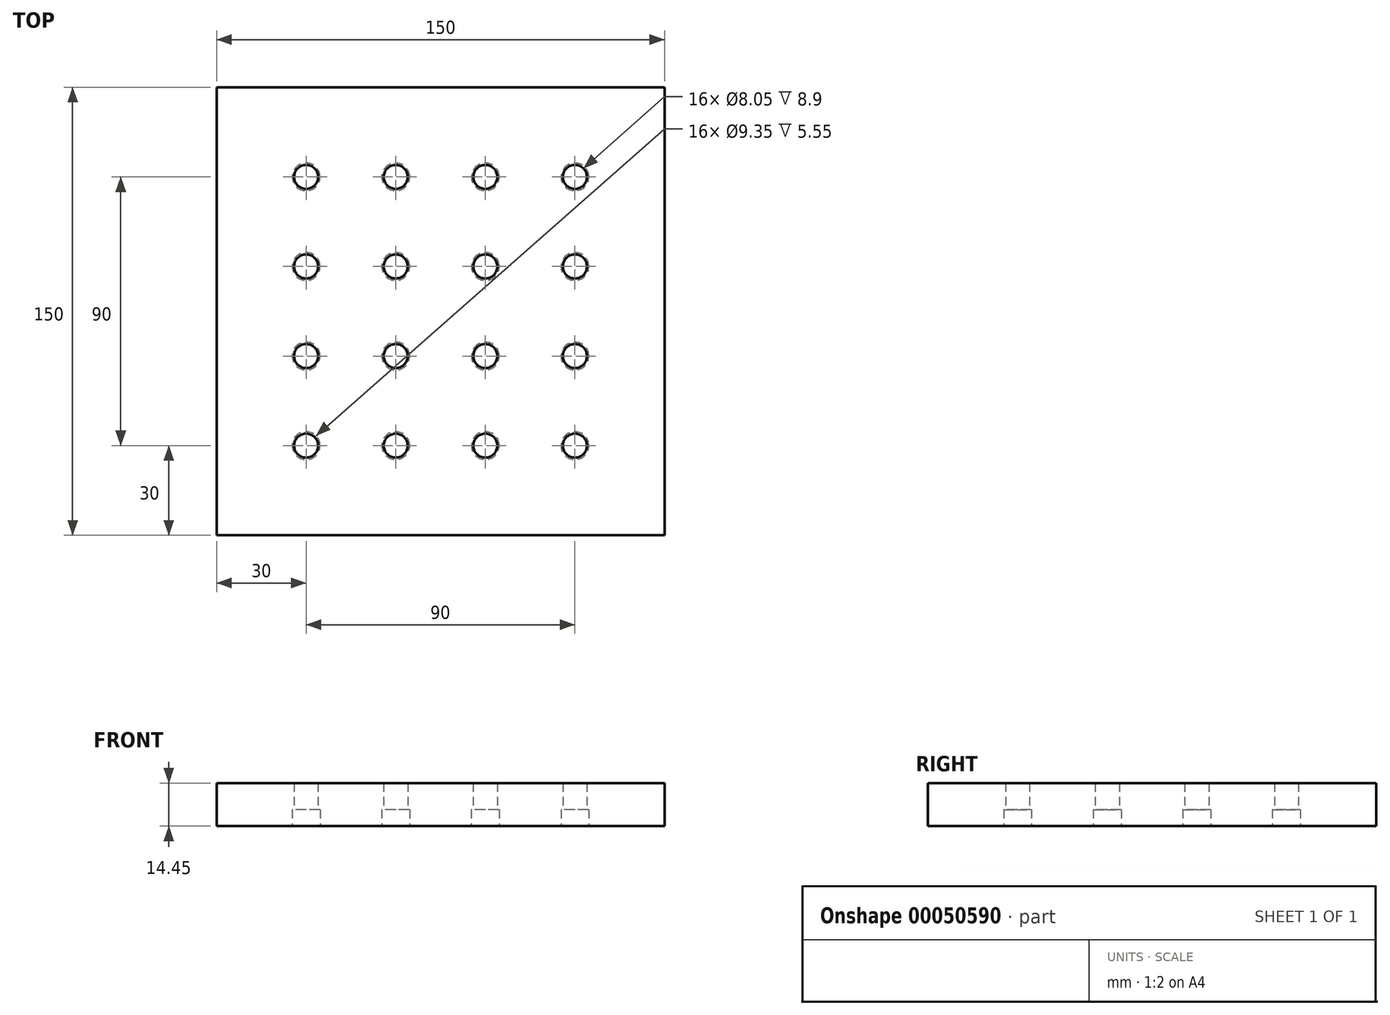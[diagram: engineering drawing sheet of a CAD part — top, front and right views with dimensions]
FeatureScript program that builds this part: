
annotation { "Feature Type Name" : "Feature", "Feature Type Description" : "" }
export const myFeature = defineFeature(function(context is Context, id is Id, definition is map)
    precondition{}
    {
        {
            var Q0;
            Q0=qCreatedBy(makeId("Top.planeOp"),FACE);
            var sketch = newSketch(context, id + "F0", { "sketchPlane" : qUnion([Q0])});
            skLineSegment(sketch, "E0.bottom", {"start": v(0, 0) * mm, "end": v(-150, 0) * mm});
            skLineSegment(sketch, "E0.top", {"start": v(0, 150) * mm, "end": v(-150, 150) * mm});
            skLineSegment(sketch, "E0.left", {"start": v(0, 0) * mm, "end": v(0, 150) * mm});
            skLineSegment(sketch, "E0.right", {"start": v(-150, 0) * mm, "end": v(-150, 150) * mm});
            skCircle(sketch, "E1", {"center": v(-120, 30) * mm, "radius": 4.68 * mm});
            skCircle(sketch, "E2", {"center": v(-120, 30) * mm, "radius": 4.03 * mm});
            skCircle(sketch, "E3.0.1.0", {"center": v(-120, 60) * mm, "radius": 4.68 * mm});
            skCircle(sketch, "E3.0.1.1", {"center": v(-120, 60) * mm, "radius": 4.03 * mm});
            skCircle(sketch, "E3.0.2.0", {"center": v(-120, 90) * mm, "radius": 4.68 * mm});
            skCircle(sketch, "E3.0.2.1", {"center": v(-120, 90) * mm, "radius": 4.03 * mm});
            skCircle(sketch, "E3.0.3.0", {"center": v(-120, 120) * mm, "radius": 4.68 * mm});
            skCircle(sketch, "E3.0.3.1", {"center": v(-120, 120) * mm, "radius": 4.03 * mm});
            skCircle(sketch, "E3.1.0.0", {"center": v(-90, 30) * mm, "radius": 4.68 * mm});
            skCircle(sketch, "E3.1.0.1", {"center": v(-90, 30) * mm, "radius": 4.03 * mm});
            skCircle(sketch, "E3.1.1.0", {"center": v(-90, 60) * mm, "radius": 4.68 * mm});
            skCircle(sketch, "E3.1.1.1", {"center": v(-90, 60) * mm, "radius": 4.03 * mm});
            skCircle(sketch, "E3.1.2.0", {"center": v(-90, 90) * mm, "radius": 4.68 * mm});
            skCircle(sketch, "E3.1.2.1", {"center": v(-90, 90) * mm, "radius": 4.03 * mm});
            skCircle(sketch, "E3.1.3.0", {"center": v(-90, 120) * mm, "radius": 4.68 * mm});
            skCircle(sketch, "E3.1.3.1", {"center": v(-90, 120) * mm, "radius": 4.03 * mm});
            skCircle(sketch, "E3.2.0.0", {"center": v(-60, 30) * mm, "radius": 4.68 * mm});
            skCircle(sketch, "E3.2.0.1", {"center": v(-60, 30) * mm, "radius": 4.03 * mm});
            skCircle(sketch, "E3.2.1.0", {"center": v(-60, 60) * mm, "radius": 4.68 * mm});
            skCircle(sketch, "E3.2.1.1", {"center": v(-60, 60) * mm, "radius": 4.03 * mm});
            skCircle(sketch, "E3.2.2.0", {"center": v(-60, 90) * mm, "radius": 4.68 * mm});
            skCircle(sketch, "E3.2.2.1", {"center": v(-60, 90) * mm, "radius": 4.03 * mm});
            skCircle(sketch, "E3.2.3.0", {"center": v(-60, 120) * mm, "radius": 4.68 * mm});
            skCircle(sketch, "E3.2.3.1", {"center": v(-60, 120) * mm, "radius": 4.03 * mm});
            skCircle(sketch, "E3.3.0.0", {"center": v(-30, 30) * mm, "radius": 4.68 * mm});
            skCircle(sketch, "E3.3.0.1", {"center": v(-30, 30) * mm, "radius": 4.03 * mm});
            skCircle(sketch, "E3.3.1.0", {"center": v(-30, 60) * mm, "radius": 4.68 * mm});
            skCircle(sketch, "E3.3.1.1", {"center": v(-30, 60) * mm, "radius": 4.03 * mm});
            skCircle(sketch, "E3.3.2.0", {"center": v(-30, 90) * mm, "radius": 4.68 * mm});
            skCircle(sketch, "E3.3.2.1", {"center": v(-30, 90) * mm, "radius": 4.03 * mm});
            skCircle(sketch, "E3.3.3.0", {"center": v(-30, 120) * mm, "radius": 4.68 * mm});
            skCircle(sketch, "E3.3.3.1", {"center": v(-30, 120) * mm, "radius": 4.03 * mm});
            skLineSegment(sketch, "E3.direction1", {"start": v(-120, 30) * mm, "end": v(-90, 30) * mm, "construction": true});
            skLineSegment(sketch, "E3.direction2", {"start": v(-120, 30) * mm, "end": v(-120, 60) * mm, "construction": true});
            skSolve(sketch);
        }
        {
            var Q0;
            Q0=makeQuery(id+"F0.imprint","IMPRINT",FACE,{"disambiguationData":[TD([[makeQuery(id+"F0.imprint","IMPRINT",EDGE,{"derivedFrom":sQuery(id+"F0.wireOp",EDGE,"E3.0.3.1")}),1.0]])]});
            var Q1;
            Q1=makeQuery(id+"F0.imprint","IMPRINT",FACE,{"disambiguationData":[TD([[makeQuery(id+"F0.imprint","IMPRINT",EDGE,{"derivedFrom":sQuery(id+"F0.wireOp",EDGE,"E3.1.3.1")}),1.0]])]});
            var Q2;
            Q2=makeQuery(id+"F0.imprint","IMPRINT",FACE,{"disambiguationData":[TD([[makeQuery(id+"F0.imprint","IMPRINT",EDGE,{"derivedFrom":sQuery(id+"F0.wireOp",EDGE,"E3.2.3.1")}),1.0]])]});
            var Q3;
            Q3=makeQuery(id+"F0.imprint","IMPRINT",FACE,{"disambiguationData":[TD([[makeQuery(id+"F0.imprint","IMPRINT",EDGE,{"derivedFrom":sQuery(id+"F0.wireOp",EDGE,"E3.3.2.1")}),1.0]])]});
            var Q4;
            Q4=makeQuery(id+"F0.imprint","IMPRINT",FACE,{"disambiguationData":[TD([[makeQuery(id+"F0.imprint","IMPRINT",EDGE,{"derivedFrom":sQuery(id+"F0.wireOp",EDGE,"E3.2.2.1")}),1.0]])]});
            var Q5;
            Q5=makeQuery(id+"F0.imprint","IMPRINT",FACE,{"disambiguationData":[TD([[makeQuery(id+"F0.imprint","IMPRINT",EDGE,{"derivedFrom":sQuery(id+"F0.wireOp",EDGE,"E3.1.2.1")}),1.0]])]});
            var Q6;
            Q6=makeQuery(id+"F0.imprint","IMPRINT",FACE,{"disambiguationData":[TD([[makeQuery(id+"F0.imprint","IMPRINT",EDGE,{"derivedFrom":sQuery(id+"F0.wireOp",EDGE,"E3.0.1.1")}),1.0]])]});
            var Q7;
            Q7=makeQuery(id+"F0.imprint","IMPRINT",FACE,{"disambiguationData":[TD([[makeQuery(id+"F0.imprint","IMPRINT",EDGE,{"derivedFrom":sQuery(id+"F0.wireOp",EDGE,"E3.1.1.1")}),1.0]])]});
            var Q8;
            Q8=makeQuery(id+"F0.imprint","IMPRINT",FACE,{"disambiguationData":[TD([[makeQuery(id+"F0.imprint","IMPRINT",EDGE,{"derivedFrom":sQuery(id+"F0.wireOp",EDGE,"E3.2.1.1")}),1.0]])]});
            var Q9;
            Q9=makeQuery(id+"F0.imprint","IMPRINT",FACE,{"disambiguationData":[TD([[makeQuery(id+"F0.imprint","IMPRINT",EDGE,{"derivedFrom":sQuery(id+"F0.wireOp",EDGE,"E3.3.1.1")}),1.0]])]});
            var Q10;
            Q10=makeQuery(id+"F0.imprint","IMPRINT",FACE,{"disambiguationData":[TD([[makeQuery(id+"F0.imprint","IMPRINT",EDGE,{"derivedFrom":sQuery(id+"F0.wireOp",EDGE,"E3.3.0.1")}),1.0]])]});
            var Q11;
            Q11=makeQuery(id+"F0.imprint","IMPRINT",FACE,{"disambiguationData":[TD([[makeQuery(id+"F0.imprint","IMPRINT",EDGE,{"derivedFrom":sQuery(id+"F0.wireOp",EDGE,"E3.2.0.1")}),1.0]])]});
            var Q12;
            Q12=makeQuery(id+"F0.imprint","IMPRINT",FACE,{"disambiguationData":[TD([[makeQuery(id+"F0.imprint","IMPRINT",EDGE,{"derivedFrom":sQuery(id+"F0.wireOp",EDGE,"E3.1.0.1")}),1.0]])]});
            var Q13;
            Q13=makeQuery(id+"F0.imprint","IMPRINT",FACE,{"disambiguationData":[TD([[makeQuery(id+"F0.imprint","IMPRINT",EDGE,{"derivedFrom":sQuery(id+"F0.wireOp",EDGE,"E3.0.3.0")}),1.0]])]});
            var Q14;
            Q14=makeQuery(id+"F0.imprint","IMPRINT",FACE,{"disambiguationData":[TD([[makeQuery(id+"F0.imprint","IMPRINT",EDGE,{"derivedFrom":sQuery(id+"F0.wireOp",EDGE,"E3.1.3.0")}),1.0]])]});
            var Q15;
            Q15=makeQuery(id+"F0.imprint","IMPRINT",FACE,{"disambiguationData":[TD([[makeQuery(id+"F0.imprint","IMPRINT",EDGE,{"derivedFrom":sQuery(id+"F0.wireOp",EDGE,"E3.1.2.0")}),1.0]])]});
            var Q16;
            Q16=makeQuery(id+"F0.imprint","IMPRINT",FACE,{"disambiguationData":[TD([[makeQuery(id+"F0.imprint","IMPRINT",EDGE,{"derivedFrom":sQuery(id+"F0.wireOp",EDGE,"E3.2.3.0")}),1.0]])]});
            var Q17;
            Q17=makeQuery(id+"F0.imprint","IMPRINT",FACE,{"disambiguationData":[TD([[makeQuery(id+"F0.imprint","IMPRINT",EDGE,{"derivedFrom":sQuery(id+"F0.wireOp",EDGE,"E3.2.2.0")}),1.0]])]});
            var Q18;
            Q18=makeQuery(id+"F0.imprint","IMPRINT",FACE,{"disambiguationData":[TD([[makeQuery(id+"F0.imprint","IMPRINT",EDGE,{"derivedFrom":sQuery(id+"F0.wireOp",EDGE,"E3.0.2.1")}),1.0]])]});
            var Q19;
            Q19=makeQuery(id+"F0.imprint","IMPRINT",FACE,{"disambiguationData":[TD([[makeQuery(id+"F0.imprint","IMPRINT",EDGE,{"derivedFrom":sQuery(id+"F0.wireOp",EDGE,"E3.0.2.0")}),1.0]])]});
            var Q20;
            Q20=makeQuery(id+"F0.imprint","IMPRINT",FACE,{"disambiguationData":[TD([[makeQuery(id+"F0.imprint","IMPRINT",EDGE,{"derivedFrom":sQuery(id+"F0.wireOp",EDGE,"E3.3.3.0")}),1.0]])]});
            var Q21;
            Q21=makeQuery(id+"F0.imprint","IMPRINT",FACE,{"disambiguationData":[TD([[makeQuery(id+"F0.imprint","IMPRINT",EDGE,{"derivedFrom":sQuery(id+"F0.wireOp",EDGE,"E3.3.3.1")}),1.0]])]});
            var Q22;
            Q22=makeQuery(id+"F0.imprint","IMPRINT",FACE,{"disambiguationData":[TD([[makeQuery(id+"F0.imprint","IMPRINT",EDGE,{"derivedFrom":sQuery(id+"F0.wireOp",EDGE,"E3.3.2.0")}),1.0]])]});
            var Q23;
            Q23=makeQuery(id+"F0.imprint","IMPRINT",FACE,{"disambiguationData":[TD([[makeQuery(id+"F0.imprint","IMPRINT",EDGE,{"derivedFrom":sQuery(id+"F0.wireOp",EDGE,"E3.0.1.0")}),1.0]])]});
            var Q24;
            Q24=makeQuery(id+"F0.imprint","IMPRINT",FACE,{"disambiguationData":[TD([[makeQuery(id+"F0.imprint","IMPRINT",EDGE,{"derivedFrom":sQuery(id+"F0.wireOp",EDGE,"E3.1.1.0")}),1.0]])]});
            var Q25;
            Q25=makeQuery(id+"F0.imprint","IMPRINT",FACE,{"disambiguationData":[TD([[makeQuery(id+"F0.imprint","IMPRINT",EDGE,{"derivedFrom":sQuery(id+"F0.wireOp",EDGE,"E3.1.0.0")}),1.0]])]});
            var Q26;
            Q26=makeQuery(id+"F0.imprint","IMPRINT",FACE,{"disambiguationData":[TD([[makeQuery(id+"F0.imprint","IMPRINT",EDGE,{"derivedFrom":sQuery(id+"F0.wireOp",EDGE,"E2")}),1.0]])]});
            var Q27;
            Q27=makeQuery(id+"F0.imprint","IMPRINT",FACE,{"disambiguationData":[TD([[makeQuery(id+"F0.imprint","IMPRINT",EDGE,{"derivedFrom":sQuery(id+"F0.wireOp",EDGE,"E1")}),1.0]])]});
            var Q28;
            Q28=makeQuery(id+"F0.imprint","IMPRINT",FACE,{"disambiguationData":[TD([[makeQuery(id+"F0.imprint","IMPRINT",EDGE,{"derivedFrom":sQuery(id+"F0.wireOp",EDGE,"E3.2.0.0")}),1.0]])]});
            var Q29;
            Q29=makeQuery(id+"F0.imprint","IMPRINT",FACE,{"disambiguationData":[TD([[makeQuery(id+"F0.imprint","IMPRINT",EDGE,{"derivedFrom":sQuery(id+"F0.wireOp",EDGE,"E3.3.0.0")}),1.0]])]});
            var Q30;
            Q30=makeQuery(id+"F0.imprint","IMPRINT",FACE,{"disambiguationData":[TD([[makeQuery(id+"F0.imprint","IMPRINT",EDGE,{"derivedFrom":sQuery(id+"F0.wireOp",EDGE,"E0.bottom")}),-1.0]])]});
            var Q31;
            Q31=makeQuery(id+"F0.imprint","IMPRINT",FACE,{"disambiguationData":[TD([[makeQuery(id+"F0.imprint","IMPRINT",EDGE,{"derivedFrom":sQuery(id+"F0.wireOp",EDGE,"E3.2.1.0")}),1.0]])]});
            var Q32;
            Q32=makeQuery(id+"F0.imprint","IMPRINT",FACE,{"disambiguationData":[TD([[makeQuery(id+"F0.imprint","IMPRINT",EDGE,{"derivedFrom":sQuery(id+"F0.wireOp",EDGE,"E3.3.1.0")}),1.0]])]});
            extrude(context, id + "F1", {"entities" : qUnion([Q0, Q1, Q2, Q3, Q4, Q5, Q6, Q7, Q8, Q9, Q10, Q11, Q12, Q13, Q14, Q15, Q16, Q17, Q18, Q19, Q20, Q21, Q22, Q23, Q24, Q25, Q26, Q27, Q28, Q29, Q30, Q31, Q32]), "depth" : 14.45 * mm});
        }
        {
            var Q0;
            Q0=makeQuery(id+"F0.imprint","IMPRINT",FACE,{"disambiguationData":[TD([[makeQuery(id+"F0.imprint","IMPRINT",EDGE,{"derivedFrom":sQuery(id+"F0.wireOp",EDGE,"E2")}),1.0]])]});
            var Q1;
            Q1=makeQuery(id+"F0.imprint","IMPRINT",FACE,{"disambiguationData":[TD([[makeQuery(id+"F0.imprint","IMPRINT",EDGE,{"derivedFrom":sQuery(id+"F0.wireOp",EDGE,"E3.1.0.1")}),1.0]])]});
            var Q2;
            Q2=makeQuery(id+"F0.imprint","IMPRINT",FACE,{"disambiguationData":[TD([[makeQuery(id+"F0.imprint","IMPRINT",EDGE,{"derivedFrom":sQuery(id+"F0.wireOp",EDGE,"E3.2.0.1")}),1.0]])]});
            var Q3;
            Q3=makeQuery(id+"F0.imprint","IMPRINT",FACE,{"disambiguationData":[TD([[makeQuery(id+"F0.imprint","IMPRINT",EDGE,{"derivedFrom":sQuery(id+"F0.wireOp",EDGE,"E3.3.0.1")}),1.0]])]});
            var Q4;
            Q4=makeQuery(id+"F0.imprint","IMPRINT",FACE,{"disambiguationData":[TD([[makeQuery(id+"F0.imprint","IMPRINT",EDGE,{"derivedFrom":sQuery(id+"F0.wireOp",EDGE,"E3.3.1.1")}),1.0]])]});
            var Q5;
            Q5=makeQuery(id+"F0.imprint","IMPRINT",FACE,{"disambiguationData":[TD([[makeQuery(id+"F0.imprint","IMPRINT",EDGE,{"derivedFrom":sQuery(id+"F0.wireOp",EDGE,"E3.2.1.1")}),1.0]])]});
            var Q6;
            Q6=makeQuery(id+"F0.imprint","IMPRINT",FACE,{"disambiguationData":[TD([[makeQuery(id+"F0.imprint","IMPRINT",EDGE,{"derivedFrom":sQuery(id+"F0.wireOp",EDGE,"E3.1.1.1")}),1.0]])]});
            var Q7;
            Q7=makeQuery(id+"F0.imprint","IMPRINT",FACE,{"disambiguationData":[TD([[makeQuery(id+"F0.imprint","IMPRINT",EDGE,{"derivedFrom":sQuery(id+"F0.wireOp",EDGE,"E3.0.1.1")}),1.0]])]});
            var Q8;
            Q8=makeQuery(id+"F0.imprint","IMPRINT",FACE,{"disambiguationData":[TD([[makeQuery(id+"F0.imprint","IMPRINT",EDGE,{"derivedFrom":sQuery(id+"F0.wireOp",EDGE,"E3.0.2.1")}),1.0]])]});
            var Q9;
            Q9=makeQuery(id+"F0.imprint","IMPRINT",FACE,{"disambiguationData":[TD([[makeQuery(id+"F0.imprint","IMPRINT",EDGE,{"derivedFrom":sQuery(id+"F0.wireOp",EDGE,"E3.1.2.1")}),1.0]])]});
            var Q10;
            Q10=makeQuery(id+"F0.imprint","IMPRINT",FACE,{"disambiguationData":[TD([[makeQuery(id+"F0.imprint","IMPRINT",EDGE,{"derivedFrom":sQuery(id+"F0.wireOp",EDGE,"E3.2.2.1")}),1.0]])]});
            var Q11;
            Q11=makeQuery(id+"F0.imprint","IMPRINT",FACE,{"disambiguationData":[TD([[makeQuery(id+"F0.imprint","IMPRINT",EDGE,{"derivedFrom":sQuery(id+"F0.wireOp",EDGE,"E3.3.2.1")}),1.0]])]});
            var Q12;
            Q12=makeQuery(id+"F0.imprint","IMPRINT",FACE,{"disambiguationData":[TD([[makeQuery(id+"F0.imprint","IMPRINT",EDGE,{"derivedFrom":sQuery(id+"F0.wireOp",EDGE,"E3.3.3.1")}),1.0]])]});
            var Q13;
            Q13=makeQuery(id+"F0.imprint","IMPRINT",FACE,{"disambiguationData":[TD([[makeQuery(id+"F0.imprint","IMPRINT",EDGE,{"derivedFrom":sQuery(id+"F0.wireOp",EDGE,"E3.2.3.1")}),1.0]])]});
            var Q14;
            Q14=makeQuery(id+"F0.imprint","IMPRINT",FACE,{"disambiguationData":[TD([[makeQuery(id+"F0.imprint","IMPRINT",EDGE,{"derivedFrom":sQuery(id+"F0.wireOp",EDGE,"E3.1.3.1")}),1.0]])]});
            var Q15;
            Q15=makeQuery(id+"F0.imprint","IMPRINT",FACE,{"disambiguationData":[TD([[makeQuery(id+"F0.imprint","IMPRINT",EDGE,{"derivedFrom":sQuery(id+"F0.wireOp",EDGE,"E3.0.3.1")}),1.0]])]});
            extrude(context, id + "F2", {"entities" : qUnion([Q0, Q1, Q2, Q3, Q4, Q5, Q6, Q7, Q8, Q9, Q10, Q11, Q12, Q13, Q14, Q15]), "operationType" : NewBodyOperationType.REMOVE, "depth" : 25 * mm});
        }
        {
            var Q0;
            Q0=makeQuery(id+"F0.imprint","IMPRINT",FACE,{"disambiguationData":[TD([[makeQuery(id+"F0.imprint","IMPRINT",EDGE,{"derivedFrom":sQuery(id+"F0.wireOp",EDGE,"E1")}),1.0]])]});
            var Q1;
            Q1=makeQuery(id+"F0.imprint","IMPRINT",FACE,{"disambiguationData":[TD([[makeQuery(id+"F0.imprint","IMPRINT",EDGE,{"derivedFrom":sQuery(id+"F0.wireOp",EDGE,"E3.1.0.0")}),1.0]])]});
            var Q2;
            Q2=makeQuery(id+"F0.imprint","IMPRINT",FACE,{"disambiguationData":[TD([[makeQuery(id+"F0.imprint","IMPRINT",EDGE,{"derivedFrom":sQuery(id+"F0.wireOp",EDGE,"E3.2.0.0")}),1.0]])]});
            var Q3;
            Q3=makeQuery(id+"F0.imprint","IMPRINT",FACE,{"disambiguationData":[TD([[makeQuery(id+"F0.imprint","IMPRINT",EDGE,{"derivedFrom":sQuery(id+"F0.wireOp",EDGE,"E3.3.0.0")}),1.0]])]});
            var Q4;
            Q4=makeQuery(id+"F0.imprint","IMPRINT",FACE,{"disambiguationData":[TD([[makeQuery(id+"F0.imprint","IMPRINT",EDGE,{"derivedFrom":sQuery(id+"F0.wireOp",EDGE,"E3.3.1.0")}),1.0]])]});
            var Q5;
            Q5=makeQuery(id+"F0.imprint","IMPRINT",FACE,{"disambiguationData":[TD([[makeQuery(id+"F0.imprint","IMPRINT",EDGE,{"derivedFrom":sQuery(id+"F0.wireOp",EDGE,"E3.2.1.0")}),1.0]])]});
            var Q6;
            Q6=makeQuery(id+"F0.imprint","IMPRINT",FACE,{"disambiguationData":[TD([[makeQuery(id+"F0.imprint","IMPRINT",EDGE,{"derivedFrom":sQuery(id+"F0.wireOp",EDGE,"E3.1.1.0")}),1.0]])]});
            var Q7;
            Q7=makeQuery(id+"F0.imprint","IMPRINT",FACE,{"disambiguationData":[TD([[makeQuery(id+"F0.imprint","IMPRINT",EDGE,{"derivedFrom":sQuery(id+"F0.wireOp",EDGE,"E3.0.1.0")}),1.0]])]});
            var Q8;
            Q8=makeQuery(id+"F0.imprint","IMPRINT",FACE,{"disambiguationData":[TD([[makeQuery(id+"F0.imprint","IMPRINT",EDGE,{"derivedFrom":sQuery(id+"F0.wireOp",EDGE,"E3.0.2.0")}),1.0]])]});
            var Q9;
            Q9=makeQuery(id+"F0.imprint","IMPRINT",FACE,{"disambiguationData":[TD([[makeQuery(id+"F0.imprint","IMPRINT",EDGE,{"derivedFrom":sQuery(id+"F0.wireOp",EDGE,"E3.1.2.0")}),1.0]])]});
            var Q10;
            Q10=makeQuery(id+"F0.imprint","IMPRINT",FACE,{"disambiguationData":[TD([[makeQuery(id+"F0.imprint","IMPRINT",EDGE,{"derivedFrom":sQuery(id+"F0.wireOp",EDGE,"E3.2.2.0")}),1.0]])]});
            var Q11;
            Q11=makeQuery(id+"F0.imprint","IMPRINT",FACE,{"disambiguationData":[TD([[makeQuery(id+"F0.imprint","IMPRINT",EDGE,{"derivedFrom":sQuery(id+"F0.wireOp",EDGE,"E3.3.2.0")}),1.0]])]});
            var Q12;
            Q12=makeQuery(id+"F0.imprint","IMPRINT",FACE,{"disambiguationData":[TD([[makeQuery(id+"F0.imprint","IMPRINT",EDGE,{"derivedFrom":sQuery(id+"F0.wireOp",EDGE,"E3.3.3.0")}),1.0]])]});
            var Q13;
            Q13=makeQuery(id+"F0.imprint","IMPRINT",FACE,{"disambiguationData":[TD([[makeQuery(id+"F0.imprint","IMPRINT",EDGE,{"derivedFrom":sQuery(id+"F0.wireOp",EDGE,"E3.2.3.0")}),1.0]])]});
            var Q14;
            Q14=makeQuery(id+"F0.imprint","IMPRINT",FACE,{"disambiguationData":[TD([[makeQuery(id+"F0.imprint","IMPRINT",EDGE,{"derivedFrom":sQuery(id+"F0.wireOp",EDGE,"E3.1.3.0")}),1.0]])]});
            var Q15;
            Q15=makeQuery(id+"F0.imprint","IMPRINT",FACE,{"disambiguationData":[TD([[makeQuery(id+"F0.imprint","IMPRINT",EDGE,{"derivedFrom":sQuery(id+"F0.wireOp",EDGE,"E3.0.3.0")}),1.0]])]});
            extrude(context, id + "F3", {"entities" : qUnion([Q0, Q1, Q2, Q3, Q4, Q5, Q6, Q7, Q8, Q9, Q10, Q11, Q12, Q13, Q14, Q15]), "operationType" : NewBodyOperationType.REMOVE, "depth" : 5.55 * mm});
        }
    });
